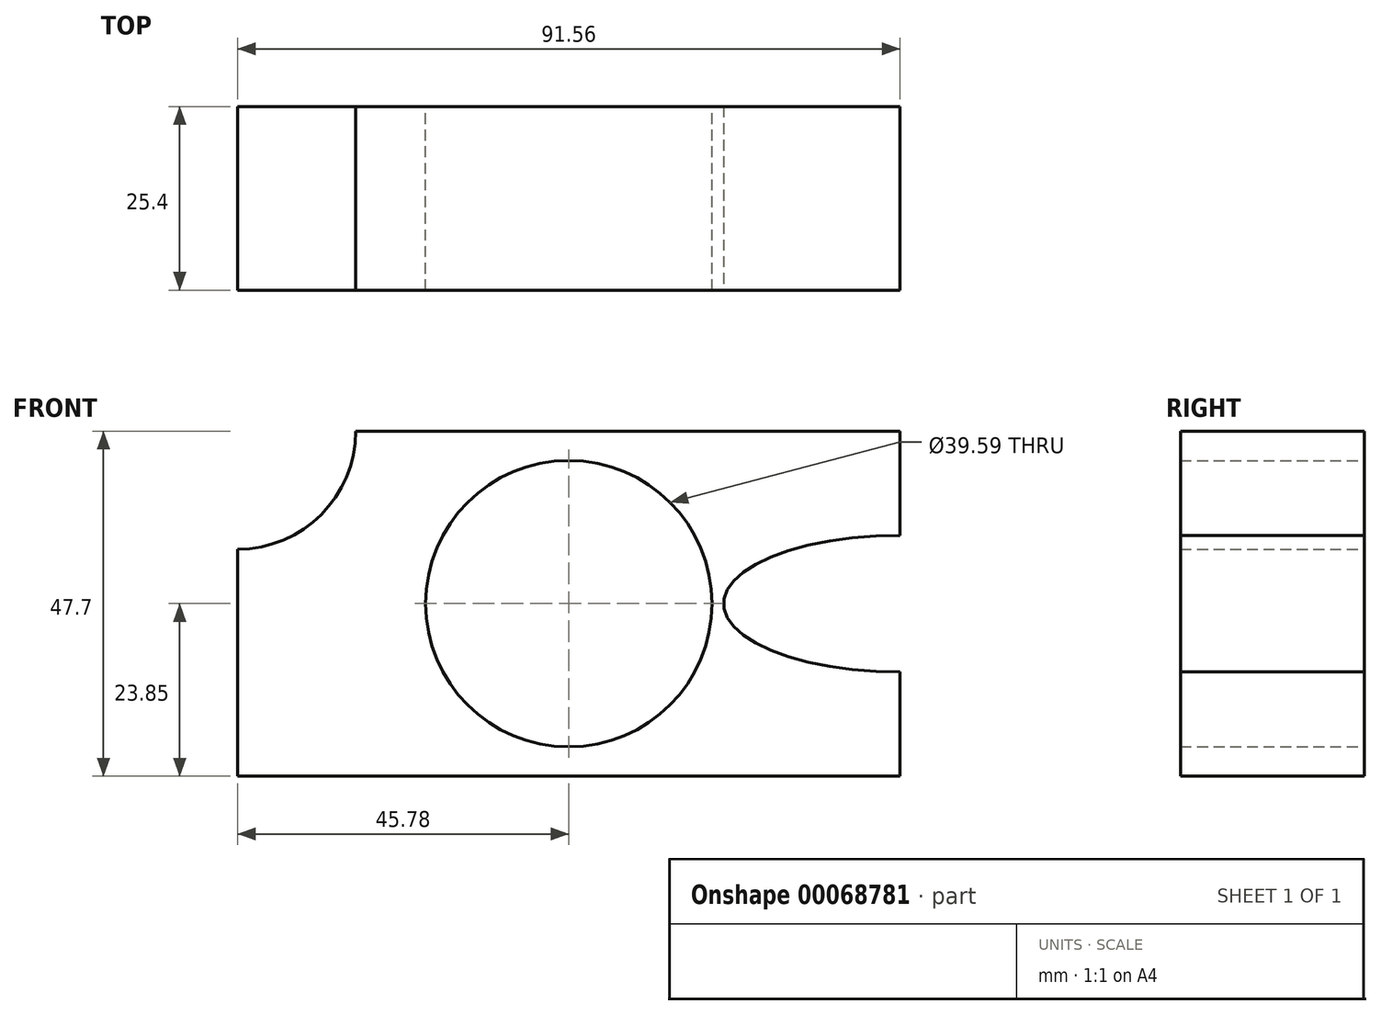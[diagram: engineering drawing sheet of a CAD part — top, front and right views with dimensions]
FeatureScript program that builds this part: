
annotation { "Feature Type Name" : "Feature", "Feature Type Description" : "" }
export const myFeature = defineFeature(function(context is Context, id is Id, definition is map)
    precondition{}
    {
        {
            var Q0;
            Q0=qCreatedBy(makeId("Front.planeOp"),FACE);
            var sketch = newSketch(context, id + "F0", { "sketchPlane" : qUnion([Q0])});
            skLineSegment(sketch, "E0", {"start": v(-45.78, 23.85) * mm, "end": v(-45.78, -23.85) * mm});
            skLineSegment(sketch, "E1", {"start": v(-45.78, -23.85) * mm, "end": v(45.78, -23.85) * mm});
            skLineSegment(sketch, "E2", {"start": v(-45.78, 23.85) * mm, "end": v(45.78, 23.85) * mm});
            skLineSegment(sketch, "E3", {"start": v(45.78, 23.85) * mm, "end": v(45.78, -23.85) * mm});
            skLineSegment(sketch, "E4", {"start": v(0, 23.85) * mm, "end": v(0, -23.85) * mm, "construction": true});
            skLineSegment(sketch, "E5", {"start": v(-45.78, 0) * mm, "end": v(45.78, 0) * mm, "construction": true});
            skLineSegment(sketch, "E6", {"start": v(-45.78, -23.85) * mm, "end": v(-104.07, -43.05) * mm});
            skLineSegment(sketch, "E7", {"start": v(-45.78, 23.85) * mm, "end": v(-104.07, 4.65) * mm});
            skLineSegment(sketch, "E8", {"start": v(-104.07, 4.65) * mm, "end": v(-104.07, -43.05) * mm});
            skCircle(sketch, "E9", {"center": v(0, 0) * mm, "radius": 19.8 * mm});
            skCircle(sketch, "E10", {"center": v(-22.9, 0) * mm, "radius": 33.06 * mm});
            skEllipse(sketch, "E11", {"center": v(45.78, 0) * mm, "majorRadius": 24.4 * mm, "minorRadius": 9.46 * mm, "majorAxis": v(1, 0)});
            skArc(sketch, "E12", {"start": v(-61.25, 29.07) * mm, "mid": v(-29.46, 23.79) * mm, "end": v(-61.3, 18.74) * mm});
            skArc(sketch, "E13", {"start": v(-41.88, 23.85) * mm, "mid": v(-63.89, 9.17) * mm, "end": v(-81.32, 29.07) * mm});
            skArc(sketch, "E14", {"start": v(-61.25, 29.07) * mm, "mid": v(-71.29, 35.42) * mm, "end": v(-81.32, 29.07) * mm});
            skSolve(sketch);
        }
        {
            var Q0;
            {var subQ0=sQuery(id+"F0.wireOp",EDGE,"E10");var subQ1=sQuery(id+"F0.wireOp",EDGE,"E2");var subQ2=makeQuery(id+"F0.imprint","INTERSECT",VERTEX,{"derivedFrom":[subQ1,subQ0]});Q0=makeQuery(id+"F0.imprint","IMPRINT",FACE,{"disambiguationData":[TD([[makeQuery(id+"F0.imprint","IMPRINT",EDGE,{"disambiguationData":[TD([[subQ2,1.0]])],"derivedFrom":subQ1}),-1.0]])]});}
            extrude(context, id + "F1", {"entities" : qUnion([Q0]), "depth" : 25.4 * mm});
        }
        {
            var Q0;
            {var subQ0=sQuery(id+"F0.wireOp",EDGE,"E3");var subQ1=sQuery(id+"F0.wireOp",EDGE,"E1");var subQ2=makeQuery(id+"F0.imprint","INTERSECT",VERTEX,{"derivedFrom":[subQ1,subQ0]});Q0=makeQuery(id+"F0.imprint","IMPRINT",FACE,{"disambiguationData":[TD([[makeQuery(id+"F0.imprint","IMPRINT",EDGE,{"disambiguationData":[TD([[subQ2,1.0]])],"derivedFrom":subQ1}),1.0]])]});}
            extrude(context, id + "F2", {"entities" : qUnion([Q0]), "operationType" : NewBodyOperationType.ADD, "depth" : 25.4 * mm});
        }
    });
